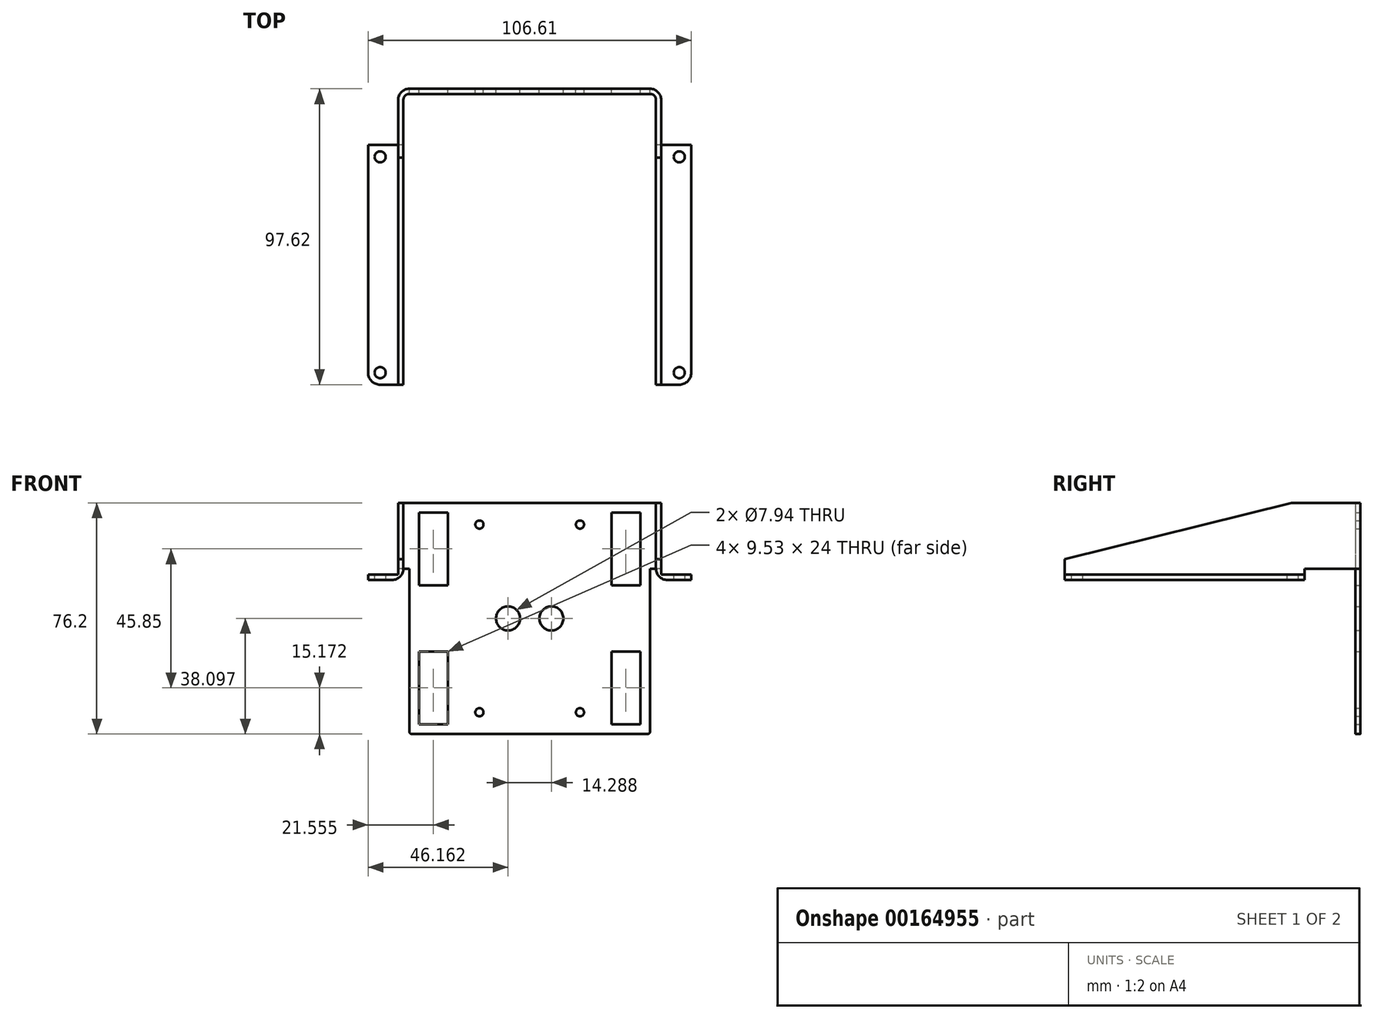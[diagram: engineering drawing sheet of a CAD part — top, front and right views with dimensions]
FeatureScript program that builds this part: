
annotation { "Feature Type Name" : "Feature", "Feature Type Description" : "" }
export const myFeature = defineFeature(function(context is Context, id is Id, definition is map)
    precondition{}
    {
        {
            var Q0;
            Q0=qCreatedBy(makeId("Top.planeOp"),FACE);
            var sketch = newSketch(context, id + "F0", { "sketchPlane" : qUnion([Q0])});
            skLineSegment(sketch, "E0.top", {"start": v(0, -95.9) * mm, "end": v(-1.7, -95.9) * mm});
            skLineSegment(sketch, "E0.left", {"start": v(0, 0) * mm, "end": v(0, -95.9) * mm});
            skLineSegment(sketch, "E0.right", {"start": v(-1.7, 1.7) * mm, "end": v(-1.7, -95.9) * mm});
            skLineSegment(sketch, "E1.bottom", {"start": v(0, 0) * mm, "end": v(83.35, 0) * mm});
            skLineSegment(sketch, "E1.top", {"start": v(-1.7, 1.7) * mm, "end": v(85.06, 1.7) * mm});
            skLineSegment(sketch, "E2.top", {"start": v(83.35, -95.9) * mm, "end": v(85.06, -95.9) * mm});
            skLineSegment(sketch, "E2.left", {"start": v(83.35, 0) * mm, "end": v(83.35, -95.9) * mm});
            skLineSegment(sketch, "E2.right", {"start": v(85.06, 1.7) * mm, "end": v(85.06, -95.9) * mm});
            skLineSegment(sketch, "E3", {"start": v(41.68, 0) * mm, "end": v(41.68, 1.7) * mm, "construction": true});
            skSolve(sketch);
        }
        {
            var Q0;
            Q0 = qSketchRegion(id + "F0", true);
            extrude(context, id + "F1", {"entities" : qUnion([Q0]), "depth" : 21.7 * mm});
        }
        {
            var Q0;
            Q0=makeQuery(id+"F1.opExtrude","CAP_FACE",FACE,{"disambiguationData":[OSD([sQuery(id+"F0.wireOp",EDGE,"E0.top"),sQuery(id+"F0.wireOp",EDGE,"E0.left"),sQuery(id+"F0.wireOp",EDGE,"E0.right"),sQuery(id+"F0.wireOp",EDGE,"E1.bottom"),sQuery(id+"F0.wireOp",EDGE,"E1.top"),sQuery(id+"F0.wireOp",EDGE,"E2.top"),sQuery(id+"F0.wireOp",EDGE,"E2.left"),sQuery(id+"F0.wireOp",EDGE,"E2.right")])],"isStart":true});
            var sketch = newSketch(context, id + "F2", { "sketchPlane" : qUnion([Q0])});
            skLineSegment(sketch, "E4.bottom", {"start": v(0, 16.8) * mm, "end": v(-1.7, 16.8) * mm});
            skLineSegment(sketch, "E4.top", {"start": v(0, 95.9) * mm, "end": v(-1.7, 95.9) * mm});
            skLineSegment(sketch, "E4.left", {"start": v(0, 16.8) * mm, "end": v(0, 95.9) * mm});
            skLineSegment(sketch, "E4.right", {"start": v(-1.7, 16.8) * mm, "end": v(-1.7, 95.9) * mm});
            skLineSegment(sketch, "E5.bottom", {"start": v(85.06, 95.9) * mm, "end": v(83.35, 95.9) * mm});
            skLineSegment(sketch, "E5.top", {"start": v(85.06, 16.8) * mm, "end": v(83.35, 16.8) * mm});
            skLineSegment(sketch, "E5.left", {"start": v(85.06, 95.9) * mm, "end": v(85.06, 16.8) * mm});
            skLineSegment(sketch, "E5.right", {"start": v(83.35, 95.9) * mm, "end": v(83.35, 16.8) * mm});
            skLineSegment(sketch, "E6", {"start": v(41.68, 0) * mm, "end": v(41.68, -7.5) * mm, "construction": true});
            skLineSegment(sketch, "E7", {"start": v(-0.85, 16.8) * mm, "end": v(-0.85, 20.76) * mm, "construction": true});
            skSolve(sketch);
        }
        {
            var Q0;
            Q0 = qSketchRegion(id + "F2", true);
            extrude(context, id + "F3", {"entities" : qUnion([Q0]), "operationType" : NewBodyOperationType.ADD, "depth" : 3.7 * mm});
        }
        {
            var Q0;
            Q0=makeQuery(id+"F3.boolean.opBoolean","MERGE",FACE,{"derivedFrom":[makeQuery(id+"F1.opExtrude","SWEPT_FACE",FACE,{"disambiguationData":[OSD([sQuery(id+"F0.wireOp",EDGE,"E2.top")])]}),makeQuery(id+"F3.opExtrude","SWEPT_FACE",FACE,{"disambiguationData":[OSD([sQuery(id+"F2.wireOp",EDGE,"E5.bottom")])]})]});
            var sketch = newSketch(context, id + "F4", { "sketchPlane" : qUnion([Q0])});
            skLineSegment(sketch, "E8.bottom", {"start": v(85.06, -3.7) * mm, "end": v(94.98, -3.7) * mm});
            skLineSegment(sketch, "E8.top", {"start": v(85.06, -1.98) * mm, "end": v(94.98, -1.98) * mm});
            skLineSegment(sketch, "E8.left", {"start": v(85.06, -3.7) * mm, "end": v(85.06, -1.98) * mm});
            skLineSegment(sketch, "E8.right", {"start": v(94.98, -3.7) * mm, "end": v(94.98, -1.98) * mm});
            skLineSegment(sketch, "E9.bottom", {"start": v(-1.7, -3.7) * mm, "end": v(-11.63, -3.7) * mm});
            skLineSegment(sketch, "E9.top", {"start": v(-1.7, -1.98) * mm, "end": v(-11.63, -1.98) * mm});
            skLineSegment(sketch, "E9.left", {"start": v(-1.7, -3.7) * mm, "end": v(-1.7, -1.98) * mm});
            skLineSegment(sketch, "E9.right", {"start": v(-11.63, -3.7) * mm, "end": v(-11.63, -1.98) * mm});
            skSolve(sketch);
        }
        {
            var Q0;
            Q0 = qSketchRegion(id + "F4", true);
            var Q1;
            Q1=makeQuery(id+"F3.opExtrude","SWEPT_FACE",FACE,{"disambiguationData":[OSD([sQuery(id+"F2.wireOp",EDGE,"E4.bottom")])]});
            extrude(context, id + "F5", {"entities" : qUnion([Q0]), "operationType" : NewBodyOperationType.ADD, "endBound" : BoundingType.UP_TO_SURFACE, "oppositeDirection" : true, "endBoundEntityFace" : qUnion([Q1]), "depth" : 25.4 * mm});
        }
        {
            var Q0;
            Q0=makeQuery(id+"F1.opExtrude","CAP_FACE",FACE,{"disambiguationData":[OSD([sQuery(id+"F0.wireOp",EDGE,"E0.top"),sQuery(id+"F0.wireOp",EDGE,"E0.left"),sQuery(id+"F0.wireOp",EDGE,"E0.right"),sQuery(id+"F0.wireOp",EDGE,"E1.bottom"),sQuery(id+"F0.wireOp",EDGE,"E1.top"),sQuery(id+"F0.wireOp",EDGE,"E2.top"),sQuery(id+"F0.wireOp",EDGE,"E2.left"),sQuery(id+"F0.wireOp",EDGE,"E2.right")])],"isStart":true});
            var sketch = newSketch(context, id + "F6", { "sketchPlane" : qUnion([Q0])});
            skLineSegment(sketch, "E10.bottom", {"start": v(81.37, 0) * mm, "end": v(1.98, 0) * mm});
            skLineSegment(sketch, "E10.top", {"start": v(81.37, -1.7) * mm, "end": v(1.98, -1.7) * mm});
            skLineSegment(sketch, "E10.left", {"start": v(81.37, 0) * mm, "end": v(81.37, -1.7) * mm});
            skLineSegment(sketch, "E10.right", {"start": v(1.98, 0) * mm, "end": v(1.98, -1.7) * mm});
            skPoint(sketch, "E11", {"position": v(41.68, -1.7) * mm});
            skArc(sketch, "E12", {"start": v(81.37, 0) * mm, "mid": v(82.77, 0.58) * mm, "end": v(83.35, 1.98) * mm, "construction": true});
            skSolve(sketch);
        }
        {
            var Q0;
            Q0 = qSketchRegion(id + "F6", true);
            extrude(context, id + "F7", {"entities" : qUnion([Q0]), "operationType" : NewBodyOperationType.ADD, "depth" : 54.5 * mm});
        }
        {
            var Q0;
            Q0=makeQuery(id+"F7.boolean.opBoolean","MERGE",FACE,{"derivedFrom":[makeQuery(id+"F1.opExtrude","SWEPT_FACE",FACE,{"disambiguationData":[OSD([sQuery(id+"F0.wireOp",EDGE,"E1.top")])]}),makeQuery(id+"F7.opExtrude","SWEPT_FACE",FACE,{"disambiguationData":[OSD([sQuery(id+"F6.wireOp",EDGE,"E10.top")])]})]});
            var sketch = newSketch(context, id + "F8", { "sketchPlane" : qUnion([Q0])});
            skLineSegment(sketch, "E13", {"start": v(-41.68, -54.5) * mm, "end": v(-41.68, 21.7) * mm, "construction": true});
            skLineSegment(sketch, "E14.bottom", {"start": v(-73.43, -39.32) * mm, "end": v(-9.93, -39.32) * mm, "construction": true});
            skLineSegment(sketch, "E14.top", {"start": v(-73.43, 6.53) * mm, "end": v(-9.93, 6.53) * mm, "construction": true});
            skLineSegment(sketch, "E14.left", {"start": v(-73.43, -39.32) * mm, "end": v(-73.43, 6.53) * mm, "construction": true});
            skLineSegment(sketch, "E14.right", {"start": v(-9.93, -39.32) * mm, "end": v(-9.93, 6.53) * mm, "construction": true});
            skPoint(sketch, "E14.middle", {"position": v(-41.68, -16.4) * mm});
            skLineSegment(sketch, "E15.bottom", {"start": v(-14.7, -27.32) * mm, "end": v(-5.16, -27.32) * mm});
            skLineSegment(sketch, "E15.top", {"start": v(-14.7, -51.32) * mm, "end": v(-5.16, -51.32) * mm});
            skLineSegment(sketch, "E15.left", {"start": v(-14.7, -27.32) * mm, "end": v(-14.7, -51.32) * mm});
            skLineSegment(sketch, "E15.right", {"start": v(-5.16, -27.32) * mm, "end": v(-5.16, -51.32) * mm});
            skPoint(sketch, "E15.middle", {"position": v(-9.93, -39.32) * mm});
            skLineSegment(sketch, "E16.bottom", {"start": v(-14.7, -5.47) * mm, "end": v(-5.16, -5.47) * mm});
            skLineSegment(sketch, "E16.top", {"start": v(-14.7, 18.53) * mm, "end": v(-5.16, 18.53) * mm});
            skLineSegment(sketch, "E16.left", {"start": v(-14.7, -5.47) * mm, "end": v(-14.7, 18.53) * mm});
            skLineSegment(sketch, "E16.right", {"start": v(-5.16, -5.47) * mm, "end": v(-5.16, 18.53) * mm});
            skPoint(sketch, "E16.middle", {"position": v(-9.93, 6.53) * mm});
            skLineSegment(sketch, "E17.bottom", {"start": v(-68.66, -5.47) * mm, "end": v(-78.2, -5.47) * mm});
            skLineSegment(sketch, "E17.top", {"start": v(-68.66, 18.53) * mm, "end": v(-78.2, 18.53) * mm});
            skLineSegment(sketch, "E17.left", {"start": v(-68.66, -5.47) * mm, "end": v(-68.66, 18.53) * mm});
            skLineSegment(sketch, "E17.right", {"start": v(-78.2, -5.47) * mm, "end": v(-78.2, 18.53) * mm});
            skPoint(sketch, "E17.middle", {"position": v(-73.43, 6.53) * mm});
            skLineSegment(sketch, "E18.bottom", {"start": v(-78.2, -51.32) * mm, "end": v(-68.66, -51.32) * mm});
            skLineSegment(sketch, "E18.top", {"start": v(-78.2, -27.32) * mm, "end": v(-68.66, -27.32) * mm});
            skLineSegment(sketch, "E18.left", {"start": v(-78.2, -51.32) * mm, "end": v(-78.2, -27.32) * mm});
            skLineSegment(sketch, "E18.right", {"start": v(-68.66, -51.32) * mm, "end": v(-68.66, -27.32) * mm});
            skPoint(sketch, "E18.middle", {"position": v(-73.43, -39.32) * mm});
            skLineSegment(sketch, "E19.bottom", {"start": v(-5.16, -51.32) * mm, "end": v(-1.98, -51.32) * mm, "construction": true});
            skLineSegment(sketch, "E19.top", {"start": v(-5.16, -54.5) * mm, "end": v(-1.98, -54.5) * mm, "construction": true});
            skLineSegment(sketch, "E19.left", {"start": v(-5.16, -51.32) * mm, "end": v(-5.16, -54.5) * mm, "construction": true});
            skLineSegment(sketch, "E19.right", {"start": v(-1.98, -51.32) * mm, "end": v(-1.98, -54.5) * mm, "construction": true});
            skLineSegment(sketch, "E20.bottom", {"start": v(-25.09, -47.35) * mm, "end": v(-58.26, -47.35) * mm, "construction": true});
            skLineSegment(sketch, "E20.top", {"start": v(-25.09, 14.56) * mm, "end": v(-58.26, 14.56) * mm, "construction": true});
            skLineSegment(sketch, "E20.left", {"start": v(-25.09, -47.35) * mm, "end": v(-25.09, 14.56) * mm, "construction": true});
            skLineSegment(sketch, "E20.right", {"start": v(-58.26, -47.35) * mm, "end": v(-58.26, 14.56) * mm, "construction": true});
            skLineSegment(sketch, "E21", {"start": v(-14.7, -51.32) * mm, "end": v(-25.09, -51.32) * mm, "construction": true});
            skLineSegment(sketch, "E22", {"start": v(-25.09, -51.32) * mm, "end": v(-25.09, -47.35) * mm, "construction": true});
            skCircle(sketch, "E23", {"center": v(-25.09, -47.35) * mm, "radius": 1.35 * mm});
            skCircle(sketch, "E24", {"center": v(-58.26, -47.35) * mm, "radius": 1.35 * mm});
            skCircle(sketch, "E25", {"center": v(-58.26, 14.56) * mm, "radius": 1.35 * mm});
            skCircle(sketch, "E26", {"center": v(-25.09, 14.56) * mm, "radius": 1.35 * mm});
            skLineSegment(sketch, "E27", {"start": v(-48.82, -16.4) * mm, "end": v(-34.53, -16.4) * mm, "construction": true});
            skCircle(sketch, "E28", {"center": v(-48.82, -16.4) * mm, "radius": 3.97 * mm});
            skCircle(sketch, "E29", {"center": v(-34.53, -16.4) * mm, "radius": 3.97 * mm});
            skSolve(sketch);
        }
        {
            var Q0;
            Q0 = qSketchRegion(id + "F8", true);
            var Q1;
            Q1=makeQuery(id+"F7.boolean.opBoolean","MERGE",FACE,{"derivedFrom":[makeQuery(id+"F1.opExtrude","SWEPT_FACE",FACE,{"disambiguationData":[OSD([sQuery(id+"F0.wireOp",EDGE,"E1.bottom")])]}),makeQuery(id+"F7.opExtrude","SWEPT_FACE",FACE,{"disambiguationData":[OSD([sQuery(id+"F6.wireOp",EDGE,"E10.bottom")])]})]});
            extrude(context, id + "F9", {"entities" : qUnion([Q0]), "operationType" : NewBodyOperationType.REMOVE, "endBound" : BoundingType.UP_TO_SURFACE, "oppositeDirection" : true, "endBoundEntityFace" : qUnion([Q1]), "depth" : 25.4 * mm});
        }
        {
            var Q0;
            Q0=makeQuery(id+"F7.opExtrude","CAP_EDGE",EDGE,{"disambiguationData":[OSD([sQuery(id+"F6.wireOp",EDGE,"E10.right")])],"isStart":false});
            var Q1;
            Q1=makeQuery(id+"F7.opExtrude","CAP_EDGE",EDGE,{"disambiguationData":[OSD([sQuery(id+"F6.wireOp",EDGE,"E10.left")])],"isStart":false});
            fillet(context, id + "F10", {"entities" : qUnion([Q0, Q1]), "radius" : 0.76 * mm, "tangentPropagation" : true, "allowEdgeOverflow" : false});
        }
        {
            var Q0;
            Q0=makeQuery(id+"F5.opExtrude","TWEAK_EDGE",EDGE,{"derivedFrom":[makeQuery(id+"F3.opExtrude","SWEPT_FACE",FACE,{"disambiguationData":[OSD([sQuery(id+"F2.wireOp",EDGE,"E4.bottom")])]}),makeQuery(id+"F4.imprint","IMPRINT",EDGE,{"derivedFrom":sQuery(id+"F4.wireOp",EDGE,"E8.right")})]});
            var Q1;
            Q1=makeQuery(id+"F5.opExtrude","CAP_EDGE",EDGE,{"disambiguationData":[OSD([sQuery(id+"F4.wireOp",EDGE,"E8.right")])],"isStart":true});
            var Q2;
            Q2=makeQuery(id+"F5.opExtrude","TWEAK_EDGE",EDGE,{"derivedFrom":[makeQuery(id+"F3.opExtrude","SWEPT_FACE",FACE,{"disambiguationData":[OSD([sQuery(id+"F2.wireOp",EDGE,"E4.bottom")])]}),makeQuery(id+"F4.imprint","IMPRINT",EDGE,{"derivedFrom":sQuery(id+"F4.wireOp",EDGE,"E9.right")})]});
            var Q3;
            Q3=makeQuery(id+"F5.opExtrude","CAP_EDGE",EDGE,{"disambiguationData":[OSD([sQuery(id+"F4.wireOp",EDGE,"E9.right")])],"isStart":true});
            fillet(context, id + "F11", {"entities" : qUnion([Q0, Q1, Q2, Q3]), "radius" : 3.97 * mm, "tangentPropagation" : true, "allowEdgeOverflow" : false});
        }
        {
            var Q0;
            Q0=makeQuery(id+"F3.opExtrude","CAP_EDGE",EDGE,{"disambiguationData":[OSD([sQuery(id+"F2.wireOp",EDGE,"E4.left")])],"isStart":false});
            var Q1;
            Q1=makeQuery(id+"F1.opExtrude","SWEPT_EDGE",EDGE,{"disambiguationData":[OSD([sQuery(id+"F0.wireOp",EDGE,"E0.right"),sQuery(id+"F0.wireOp",EDGE,"E1.top")])]});
            var Q2;
            Q2=makeQuery(id+"F1.opExtrude","SWEPT_EDGE",EDGE,{"disambiguationData":[OSD([sQuery(id+"F0.wireOp",EDGE,"E1.top"),sQuery(id+"F0.wireOp",EDGE,"E2.right")])]});
            var Q3;
            Q3=makeQuery(id+"F3.opExtrude","CAP_EDGE",EDGE,{"disambiguationData":[OSD([sQuery(id+"F2.wireOp",EDGE,"E5.right")])],"isStart":false});
            fillet(context, id + "F12", {"entities" : qUnion([Q0, Q1, Q2, Q3]), "radius" : 3.7 * mm, "tangentPropagation" : true, "allowEdgeOverflow" : false});
        }
        {
            var Q0;
            Q0=makeQuery(id+"F1.opExtrude","SWEPT_EDGE",EDGE,{"disambiguationData":[OSD([sQuery(id+"F0.wireOp",EDGE,"E1.bottom"),sQuery(id+"F0.wireOp",EDGE,"E2.left")])]});
            var Q1;
            Q1=makeQuery(id+"F1.opExtrude","SWEPT_EDGE",EDGE,{"disambiguationData":[OSD([sQuery(id+"F0.wireOp",EDGE,"E0.left"),sQuery(id+"F0.wireOp",EDGE,"E1.bottom")])]});
            var Q2;
            Q2=makeQuery(id+"F5.opExtrude","SWEPT_EDGE",EDGE,{"disambiguationData":[OSD([sQuery(id+"F0.wireOp",EDGE,"E2.top"),sQuery(id+"F0.wireOp",EDGE,"E2.right"),sQuery(id+"F2.wireOp",EDGE,"E5.bottom"),sQuery(id+"F2.wireOp",EDGE,"E5.left"),sQuery(id+"F4.wireOp",EDGE,"E8.top"),sQuery(id+"F4.wireOp",EDGE,"E8.left")])]});
            var Q3;
            Q3=makeQuery(id+"F5.opExtrude","SWEPT_EDGE",EDGE,{"disambiguationData":[OSD([sQuery(id+"F4.wireOp",EDGE,"E9.top"),sQuery(id+"F4.wireOp",EDGE,"E9.left")])]});
            fillet(context, id + "F13", {"entities" : qUnion([Q0, Q1, Q2, Q3]), "radius" : 1.98 * mm, "tangentPropagation" : true, "allowEdgeOverflow" : false});
        }
        {
            var Q0;
            Q0=makeQuery(id+"F3.boolean.opBoolean","MERGE",FACE,{"derivedFrom":[makeQuery(id+"F1.opExtrude","SWEPT_FACE",FACE,{"disambiguationData":[OSD([sQuery(id+"F0.wireOp",EDGE,"E0.right")])]}),makeQuery(id+"F3.opExtrude","SWEPT_FACE",FACE,{"disambiguationData":[OSD([sQuery(id+"F2.wireOp",EDGE,"E4.right")])]})]});
            var sketch = newSketch(context, id + "F14", { "sketchPlane" : qUnion([Q0])});
            skLineSegment(sketch, "E30.bottom", {"start": v(21.03, 21.7) * mm, "end": v(95.9, 21.7) * mm});
            skLineSegment(sketch, "E30.top", {"start": v(21.03, 3.17) * mm, "end": v(95.9, 3.17) * mm, "construction": true});
            skLineSegment(sketch, "E30.left", {"start": v(21.03, 21.7) * mm, "end": v(21.03, 3.17) * mm, "construction": true});
            skLineSegment(sketch, "E30.right", {"start": v(95.9, 21.7) * mm, "end": v(95.9, 3.17) * mm});
            skLineSegment(sketch, "E31", {"start": v(1.98, 21.7) * mm, "end": v(21.03, 21.7) * mm, "construction": true});
            skLineSegment(sketch, "E32", {"start": v(95.9, 0) * mm, "end": v(95.9, 3.17) * mm, "construction": true});
            skLineSegment(sketch, "E33", {"start": v(21.03, 21.7) * mm, "end": v(95.9, 3.17) * mm});
            skSolve(sketch);
        }
        {
            var Q0;
            Q0 = qSketchRegion(id + "F14", true);
            var Q1;
            Q1=makeQuery(id+"F3.boolean.opBoolean","MERGE",FACE,{"derivedFrom":[makeQuery(id+"F1.opExtrude","SWEPT_FACE",FACE,{"disambiguationData":[OSD([sQuery(id+"F0.wireOp",EDGE,"E2.right")])]}),makeQuery(id+"F3.opExtrude","SWEPT_FACE",FACE,{"disambiguationData":[OSD([sQuery(id+"F2.wireOp",EDGE,"E5.left")])]})]});
            extrude(context, id + "F15", {"entities" : qUnion([Q0]), "operationType" : NewBodyOperationType.REMOVE, "endBound" : BoundingType.UP_TO_SURFACE, "oppositeDirection" : true, "endBoundEntityFace" : qUnion([Q1]), "depth" : 25.4 * mm});
        }
        {
            var Q0;
            Q0=makeQuery(id+"F5.boolean.opBoolean","MERGE",FACE,{"derivedFrom":[makeQuery(id+"F3.opExtrude","CAP_FACE",FACE,{"disambiguationData":[OSD([sQuery(id+"F2.wireOp",EDGE,"E4.bottom"),sQuery(id+"F2.wireOp",EDGE,"E4.top"),sQuery(id+"F2.wireOp",EDGE,"E4.left"),sQuery(id+"F2.wireOp",EDGE,"E4.right")])],"isStart":false}),makeQuery(id+"F5.opExtrude","SWEPT_FACE",FACE,{"disambiguationData":[OSD([sQuery(id+"F4.wireOp",EDGE,"E9.bottom")])]})]});
            var sketch = newSketch(context, id + "F16", { "sketchPlane" : qUnion([Q0])});
            skCircle(sketch, "E34", {"center": v(-7.66, 91.94) * mm, "radius": 1.83 * mm});
            skCircle(sketch, "E35", {"center": v(-7.66, 20.76) * mm, "radius": 1.83 * mm});
            skCircle(sketch, "E36", {"center": v(91.01, 91.94) * mm, "radius": 1.83 * mm});
            skCircle(sketch, "E37", {"center": v(91.01, 20.76) * mm, "radius": 1.83 * mm});
            skSolve(sketch);
        }
        {
            var Q0;
            Q0 = qSketchRegion(id + "F16", true);
            var Q1;
            Q1=makeQuery(id+"F5.opExtrude","SWEPT_FACE",FACE,{"disambiguationData":[OSD([sQuery(id+"F4.wireOp",EDGE,"E8.top")])]});
            extrude(context, id + "F17", {"entities" : qUnion([Q0]), "operationType" : NewBodyOperationType.REMOVE, "endBound" : BoundingType.UP_TO_SURFACE, "oppositeDirection" : true, "endBoundEntityFace" : qUnion([Q1]), "depth" : 25.4 * mm});
        }
    });
